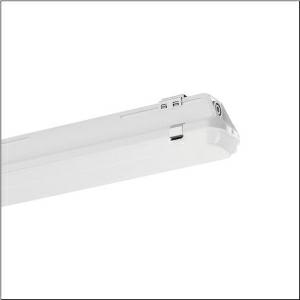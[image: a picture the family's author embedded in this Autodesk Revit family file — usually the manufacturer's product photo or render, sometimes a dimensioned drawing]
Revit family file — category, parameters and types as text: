
# Revit family: monsun_21_51fb107p430k005
name_source: partatom
category: Lighting Fixtures
units: mm (PartAtom-declared; Revit-internal decimal feet)

## family parameters
Cut with Voids When Loaded = No
Host = Face
Light Source = No
Part Type = Normal
Room Calculation Point = No
Round Connector Dimension = Use Diameter
Shared = No

## types (1)
- Monsun 21 (1 x LED, 3940 lm, 22.1 W, 4000K)
    Apparent Load = 22 VA
    CIE Flux Codes = 47 77 93 94 100
    Color Rendering = 80
    Color Temperature = 4000K
    Default Elevation = 1800 mm
    Description = Monsun 21, damp-proof luminaire, chain hanger, primary optical cover: enclosure, of PMMA, light emission: direct distribution, primary light characteristic: symmetric, installation type: suspended mounting, surface-mounted, horizontal mounting, vertical mounting, LED, rated luminous flux: 3.940lm, luminous efficacy: 178lm/W, light colour: 840, colour temperature: 4000K, control gear: ON/OFF, with terminal, 3-pole, max. 2.5mm², through-wiring: 5x 2.5mm², mains connection: 220..240V, AC, 50/60Hz, rated input power: 22W, housing, of glass-fibre reinforced polyester, uncoated, bright grey, incl. chain hanger, length: 1.590mm, width: 90mm, height: 88mm, clip for enclosure, of stainless steel (V2A), ceiling mounting element, of stainless steel (V2A), chain hanger, of stainless steel (V2A), protection rating (complete): IP66, insulation class (complete): insulation class I (protective earthing), certification: CE, ENEC, VDE, UKCA, protection symbol: D, impact resistance: IK04, permissible operating ambient temperature: -25..+35°C, standard: EN 50419, EN 60598-2-1, corresponds to IFS (International Featured Standards) requirements for safety and quality in the food industry, for indoor or canopied outdoor use, no direct snow, no direct sun, no direct rain, LABS conformity tested according to VDMA 24364:2018-05, contact your sales advisor before using the luminaires in applications with unclear chemical exposure, large temperature fluctuations or condensation-forming humidity, packaging unit: 1 piece
    Height = 89 mm
    Lamp = 1 x LED
    Lamp Light Flux = 3940 lm
    Lamp Power = 22.1 W
    Lamp count = 1
    Length = 1590 mm
    Luminous efficacy = 178 lm/W
    Manufacturer = Siteco
    ModVariant = No
    Model = 51FB107P430K005
    Mounting Place = Ceiling
    Mounting Type = Surface mounted
    Number of Poles = 1
    OnlyDefault = Yes
    Power Factor = 1
    Product Name = Monsun 21
    Product group = damp-proof luminaire
    ProductGroupID = 300
    Protection Class = Protection class I
    Protection Degree = IP 66
    RLX_Detail_Level = 1
    RLX_Emergency_Light_Flux = 0 lm
    RLX_Emergency_Type = 0
    RLX_Emergency_Type_DB = No
    RlxData = <blob elided: 88745 chars, md5=2ec45a9c>
    Socket = socket
    Standby Power = 0 W
    System Light Flux = 3940 lm
    System Power = 22 W
    Type Comments = Product without accessories
    Type Image = l_1319656.jpg
    URL = http://relux.com
    VarID = ---
    Voltage = 0 V
    Weight = 0.00 kg
    Width = 90 mm

## geometry (parser evidence)
native form markers: Blend x4, Sweep x15
no freeform markers — native parametric forms only
